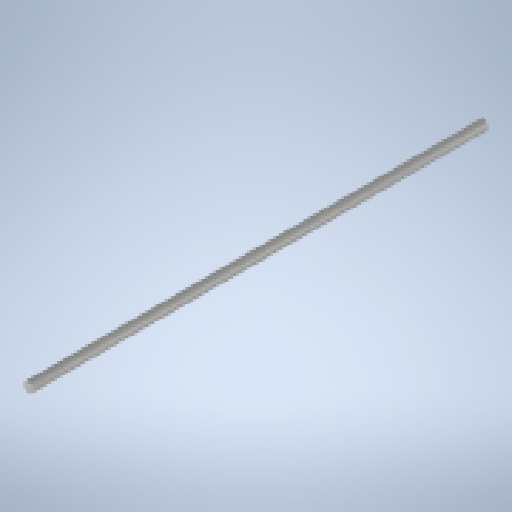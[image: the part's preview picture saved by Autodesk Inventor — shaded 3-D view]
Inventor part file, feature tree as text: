
AUTODESK INVENTOR PART (.ipt)
format: ipt  version: 2024 (Build 280153000, 153)  size: 245,760 bytes
history: native  units: mm
features: extrude x1, chamfer x1, sketch x1
ambient origin geometry x8: Origin, YZ Plane, XZ Plane, XY Plane, X Axis, Y Axis, Z Axis, Center Point
bodies: Solid1 (feature_tree)
feature tree (3):
  extrude  "Extrusion1"  Depth=365.0mm TaperAngle=0.0deg
  chamfer  "Chamfer1"  Distance=0.5mm Angle=45.0deg
  sketch  "Sketch1"  dims[d0=8.0mm d1=365.0mm d2=0.0mm d3=0.5mm d4=2.0mm d5=45.0deg]
